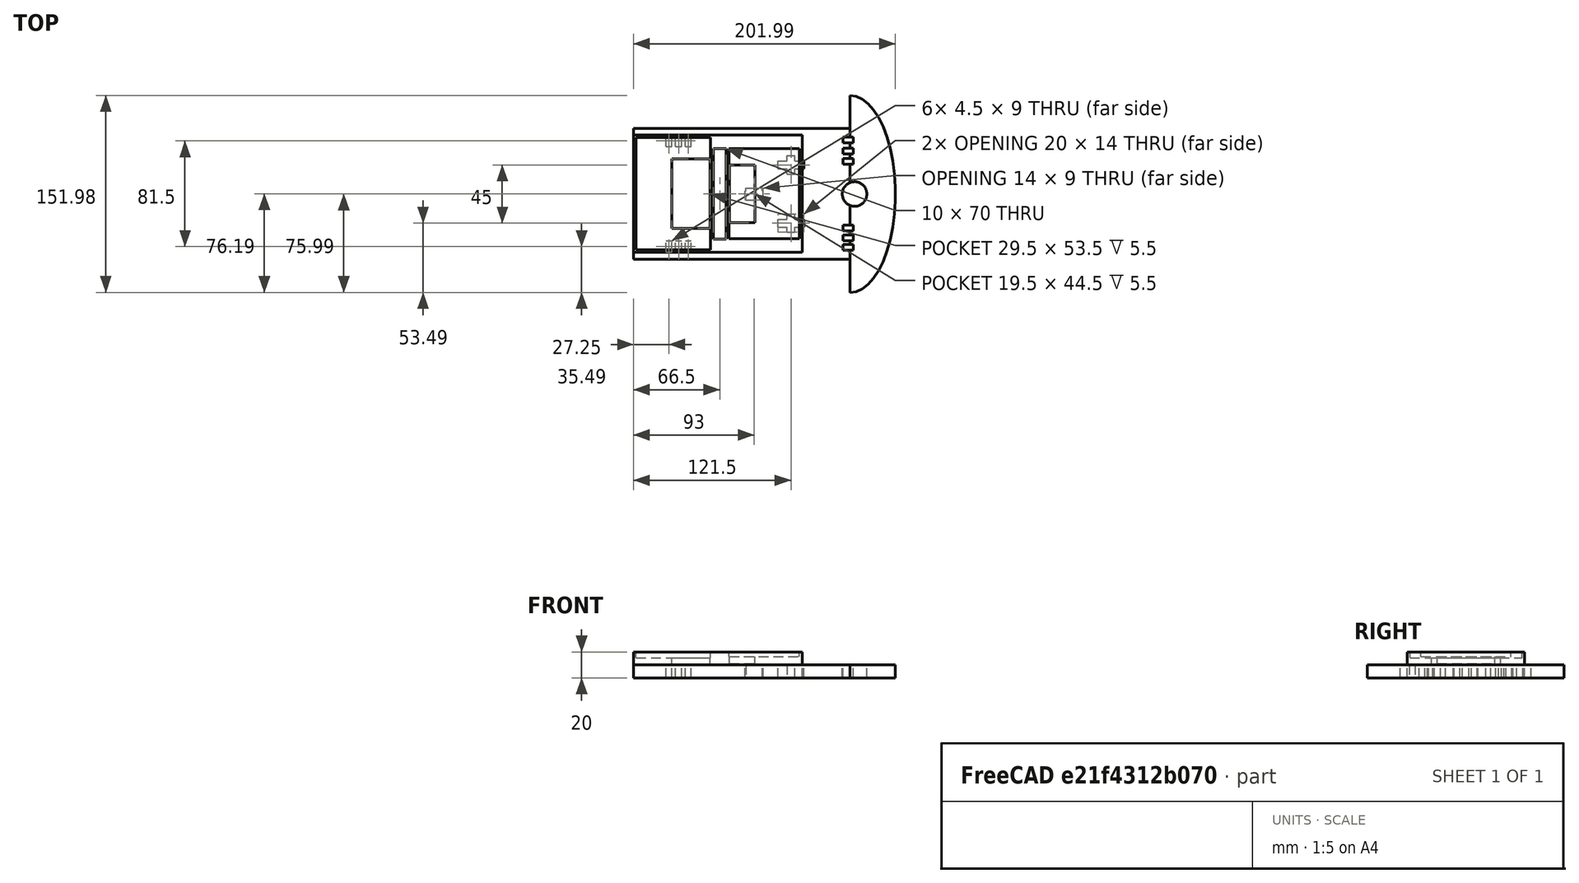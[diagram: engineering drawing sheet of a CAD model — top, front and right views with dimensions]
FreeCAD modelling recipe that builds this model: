
FCSTD DOCUMENT  (FreeCAD 0.18R16131 (Git))
Label: Chassis with Seats
License: All rights reserved
LicenseURL: http://en.wikipedia.org/wiki/All_rights_reserved
objects: Part::Box×26, Part::Fuse×3, Part::FeaturePython×2, Part::Cylinder×1, Sketcher::SketchObject×1, PartDesign::Pad×1, PartDesign::Body×1, Part::MultiCommon×1
note: 37 computed .brp shape members not serialized (recipe doc carries the construction recipe); baked Part::Feature solids carry a one-line shape summary decoded from their .brp

FEATURE [Part::Box] Box  label="Cubo"
  AttacherType = Attacher::AttachEngine3D
  Height = 10
  Length = 167
  Width = 101
FEATURE [Part::Box] Box001  label="Cubo001"
  AttacherType = Attacher::AttachEngine3D
  Height = 10
  Length = 35
  Placement = pos=(167,-25.5,0) rot=(0,0,1;0rad)
  Width = 152
FEATURE [Part::Cylinder] Cylinder  label="Cilindro"
  Angle = 360
  AttacherType = Attacher::AttachEngine3D
  Height = 10
  Placement = pos=(170.5,50.5,0) rot=(0,0,1;0rad)
  Radius = 9.5
FEATURE [Part::Box] Box002  label="Cubo002"
  AttacherType = Attacher::AttachEngine3D
  Height = 10
  Length = 14
  Placement = pos=(0,2,0) rot=(0,0,1;0rad)
  Width = 5
FEATURE [Part::Box] Box003  label="Cubo003"
  AttacherType = Attacher::AttachEngine3D
  Height = 10
  Length = 13
  Placement = pos=(0.5,0,0) rot=(0,0,1;0rad)
  Width = 9
FEATURE [Part::Fuse] Fusion
  Base = -> Box002
  Placement = pos=(86,46,0) rot=(0,0,1;0rad)
  Tool = -> Box003
FEATURE [Sketcher::SketchObject] Sketch
  MapMode = 5
  Support = -> [XY_Plane]
  sketch-geometry (1):
    g0: Ellipse CenterX=0 CenterY=0 CenterZ=0 NormalX=0 NormalY=0 NormalZ=1 MajorRadius=75.9942 MinorRadius=34.993 AngleXU=1.57073
  constraints (1):
    c: Coincident(g0,g-1)
FEATURE [PartDesign::Pad] Pad
  Length = 10
  Length2 = 100
  Profile = -> Sketch
  Type = 0
FEATURE [PartDesign::Body] Body
  Group = -> [Sketch,Pad]
  Origin = -> Origin
  Placement = pos=(167,50.5,0) rot=(0,0,1;0rad)
  Tip = -> Pad
FEATURE [Part::MultiCommon] Common
  Shapes = -> [Body,Box001]
FEATURE [Part::Box] Box004  label="Cubo004"
  AttacherType = Attacher::AttachEngine3D
  Height = 10
  Length = 20
  Placement = pos=(0,4,0) rot=(0,0,1;0rad)
  Width = 6
FEATURE [Part::Box] Box005  label="Cubo005"
  AttacherType = Attacher::AttachEngine3D
  Height = 10
  Length = 6
  Placement = pos=(7,0,0) rot=(0,0,1;0rad)
  Width = 14
FEATURE [Part::Fuse] Fusion001
  Base = -> Box004
  Placement = pos=(111.5,66,0) rot=(0,0,1;0rad)
  Tool = -> Box005
FEATURE [Part::Box] Box006  label="Cubo006"
  AttacherType = Attacher::AttachEngine3D
  Height = 10
  Length = 6
  Placement = pos=(7,0,0) rot=(0,0,1;0rad)
  Width = 14
FEATURE [Part::Box] Box007  label="Cubo007"
  AttacherType = Attacher::AttachEngine3D
  Height = 10
  Length = 20
  Placement = pos=(0,4,0) rot=(0,0,1;0rad)
  Width = 6
FEATURE [Part::Fuse] Fusion002
  Base = -> Box007
  Placement = pos=(111.5,21,0) rot=(0,0,1;0rad)
  Tool = -> Box006
FEATURE [Part::Box] Box008  label="Cubo008"
  AttacherType = Attacher::AttachEngine3D
  Height = 10
  Length = 8
  Placement = pos=(161.5,7,0) rot=(0,0,1;0rad)
  Width = 4.5
FEATURE [Part::Box] Box009  label="Cubo009"
  AttacherType = Attacher::AttachEngine3D
  Height = 10
  Length = 8
  Placement = pos=(161.5,14.5,0) rot=(0,0,1;0rad)
  Width = 4.5
FEATURE [Part::Box] Box010  label="Cubo010"
  AttacherType = Attacher::AttachEngine3D
  Height = 10
  Length = 8
  Placement = pos=(161.5,22,0) rot=(0,0,1;0rad)
  Width = 4.5
FEATURE [Part::Box] Box011  label="Cubo011"
  AttacherType = Attacher::AttachEngine3D
  Height = 10
  Length = 8
  Placement = pos=(161.5,90,0) rot=(0,0,1;0rad)
  Width = 4.5
FEATURE [Part::Box] Box012  label="Cubo012"
  AttacherType = Attacher::AttachEngine3D
  Height = 10
  Length = 8
  Placement = pos=(161.5,81.5,0) rot=(0,0,1;0rad)
  Width = 4.5
FEATURE [Part::Box] Box013  label="Cubo013"
  AttacherType = Attacher::AttachEngine3D
  Height = 10
  Length = 8
  Placement = pos=(161.5,73.5,0) rot=(0,0,1;0rad)
  Width = 4.5
FEATURE [Part::Box] Box014  label="Cubo014"
  AttacherType = Attacher::AttachEngine3D
  Height = 10
  Length = 4.5
  Placement = pos=(25,5.5,0) rot=(0,0,1;0rad)
  Width = 9
FEATURE [Part::Box] Box015  label="Cubo015"
  AttacherType = Attacher::AttachEngine3D
  Height = 10
  Length = 4.5
  Placement = pos=(32.5,5.5,0) rot=(0,0,1;0rad)
  Width = 9
FEATURE [Part::Box] Box016  label="Cubo016"
  AttacherType = Attacher::AttachEngine3D
  Height = 10
  Length = 4.5
  Placement = pos=(40,5.5,0) rot=(0,0,1;0rad)
  Width = 9
FEATURE [Part::Box] Box017  label="Cubo017"
  AttacherType = Attacher::AttachEngine3D
  Height = 10
  Length = 4.5
  Placement = pos=(25,87,0) rot=(0,0,1;0rad)
  Width = 9
FEATURE [Part::Box] Box018  label="Cubo018"
  AttacherType = Attacher::AttachEngine3D
  Height = 10
  Length = 4.5
  Placement = pos=(32.5,87,0) rot=(0,0,1;0rad)
  Width = 9
FEATURE [Part::Box] Box019  label="Cubo019"
  AttacherType = Attacher::AttachEngine3D
  Height = 10
  Length = 4.5
  Placement = pos=(40,87,0) rot=(0,0,1;0rad)
  Width = 9
FEATURE [Part::FeaturePython] XOR  label="Chassi"  # WARN: FeaturePython — macro-defined, semantics opaque (R4)
  Objects = -> [Box008,Cylinder,Box,Box012,Box009,Box010,Box011,Box013,Box014,Box015,Box016,Box017,Fusion,Common,Fusion001,Fusion002,Box018,Box019]
  Tolerance = 0
FEATURE [Part::Box] Box020  label="buraco"
  AttacherType = Attacher::AttachEngine3D
  Height = 20
  Length = 10
  Placement = pos=(61.5,10.2,0) rot=(0,0,1;0rad)
  Width = 70
FEATURE [Part::Box] Box021  label="Arduino"
  AttacherType = Attacher::AttachEngine3D
  Height = 3.5
  Length = 54.5
  Placement = pos=(73.5,10.5,16.5) rot=(0,0,1;0rad)
  Width = 69.5
FEATURE [Part::Box] Box022  label="ESP"
  AttacherType = Attacher::AttachEngine3D
  Height = 5.5
  Length = 29.5
  Placement = pos=(29.5,18.5,10) rot=(0,0,1;0rad)
  Width = 53.5
FEATURE [Part::Box] Box023  label="Cubo020"
  AttacherType = Attacher::AttachEngine3D
  Height = 20
  Length = 130
  Width = 90.5
FEATURE [Part::Box] Box024  label="RASP"
  AttacherType = Attacher::AttachEngine3D
  Height = 4.5
  Length = 57.5
  Placement = pos=(2,2,15.5) rot=(0,0,1;0rad)
  Width = 86.5
FEATURE [Part::Box] Box025  label="Arduino_nano"
  AttacherType = Attacher::AttachEngine3D
  Height = 5.5
  Length = 19.5
  Placement = pos=(74,23,11) rot=(0,0,1;0rad)
  Width = 44.5
FEATURE [Part::FeaturePython] XOR001  label="Seats"  # WARN: FeaturePython — macro-defined, semantics opaque (R4)
  Objects = -> [Box023,Box020,Box021,Box022,Box024,Box025]
  Placement = pos=(0,5.5,0) rot=(0,0,1;0rad)
  Tolerance = 0
